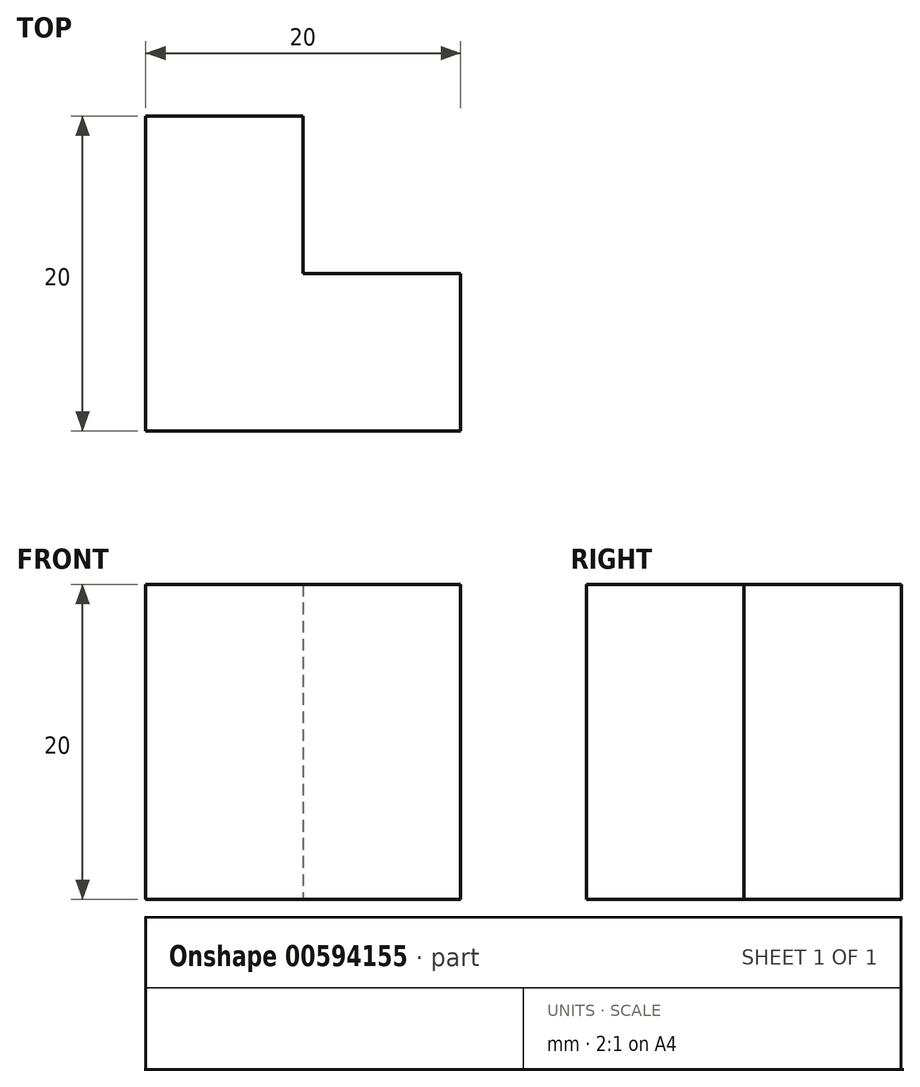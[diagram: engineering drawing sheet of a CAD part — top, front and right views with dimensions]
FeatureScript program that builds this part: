
annotation { "Feature Type Name" : "Feature", "Feature Type Description" : "" }
export const myFeature = defineFeature(function(context is Context, id is Id, definition is map)
    precondition{}
    {
        {
            var Q0;
            Q0=qCreatedBy(makeId("Top.planeOp"),FACE);
            var sketch = newSketch(context, id + "F0", { "sketchPlane" : qUnion([Q0])});
            skLineSegment(sketch, "E0", {"start": v(0, 20) * mm, "end": v(0, 0) * mm});
            skLineSegment(sketch, "E1", {"start": v(0, 0) * mm, "end": v(20, 0) * mm});
            skLineSegment(sketch, "E2", {"start": v(20, 0) * mm, "end": v(20, 10) * mm});
            skLineSegment(sketch, "E3", {"start": v(20, 10) * mm, "end": v(10, 10) * mm});
            skLineSegment(sketch, "E4", {"start": v(10, 10) * mm, "end": v(10, 20) * mm});
            skLineSegment(sketch, "E5", {"start": v(10, 20) * mm, "end": v(0, 20) * mm});
            skSolve(sketch);
        }
        {
            var Q0;
            Q0 = qSketchRegion(id + "F0", true);
            extrude(context, id + "F1", {"entities" : qUnion([Q0]), "depth" : 20 * mm, "offsetDistance" : 25 * mm});
        }
    });
